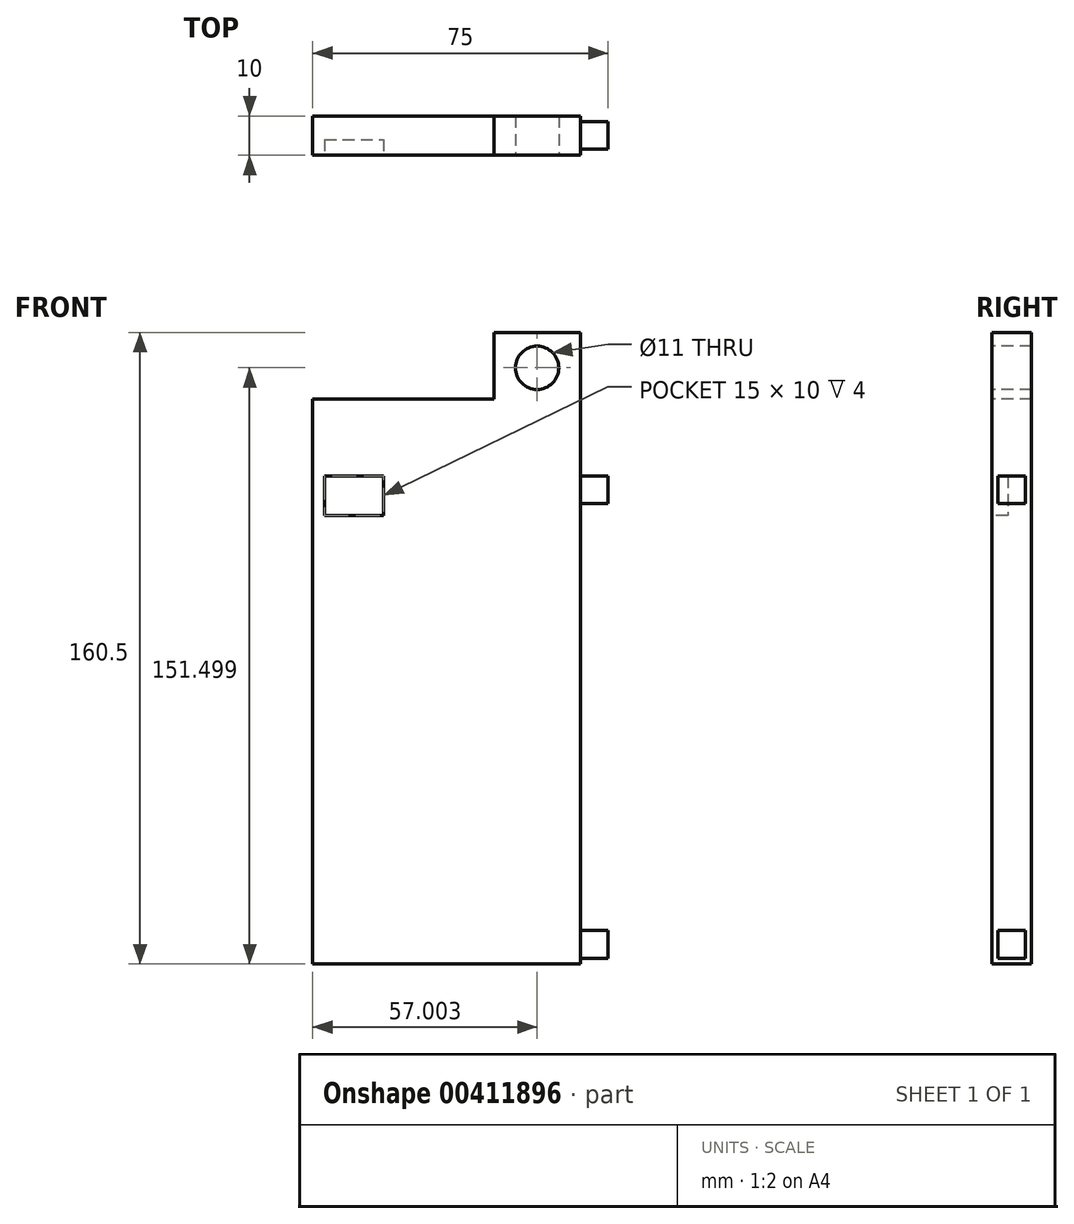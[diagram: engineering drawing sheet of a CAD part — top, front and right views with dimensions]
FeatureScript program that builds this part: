
annotation { "Feature Type Name" : "Feature", "Feature Type Description" : "" }
export const myFeature = defineFeature(function(context is Context, id is Id, definition is map)
    precondition{}
    {
        {
            var Q0;
            Q0=qCreatedBy(makeId("Front.planeOp"),FACE);
            var sketch = newSketch(context, id + "F0", { "sketchPlane" : qUnion([Q0])});
            skLineSegment(sketch, "E0.bottom", {"start": v(-29.83, 107.13) * mm, "end": v(38.17, 107.13) * mm});
            skLineSegment(sketch, "E0.top", {"start": v(-29.83, -53.37) * mm, "end": v(38.17, -53.37) * mm});
            skLineSegment(sketch, "E0.left", {"start": v(-29.83, 107.13) * mm, "end": v(-29.83, -53.37) * mm});
            skLineSegment(sketch, "E0.right", {"start": v(38.17, 107.13) * mm, "end": v(38.17, -53.37) * mm});
            skSolve(sketch);
        }
        {
            var Q0;
            Q0=makeQuery(id+"F0.imprint","IMPRINT",FACE,{"disambiguationData":[TD([[makeQuery(id+"F0.imprint","IMPRINT",EDGE,{"derivedFrom":sQuery(id+"F0.wireOp",EDGE,"E0.bottom")}),-1.0]])]});
            extrude(context, id + "F1", {"entities" : qUnion([Q0]), "depth" : 10 * mm});
        }
        {
            var Q0;
            Q0=makeQuery(id+"F1.opExtrude","CAP_FACE",FACE,{"disambiguationData":[OSD([sQuery(id+"F0.wireOp",EDGE,"E0.bottom"),sQuery(id+"F0.wireOp",EDGE,"E0.top"),sQuery(id+"F0.wireOp",EDGE,"E0.left"),sQuery(id+"F0.wireOp",EDGE,"E0.right")])],"isStart":false});
            var sketch = newSketch(context, id + "F2", { "sketchPlane" : qUnion([Q0])});
            skLineSegment(sketch, "E1.bottom", {"start": v(-29.83, 107.13) * mm, "end": v(16.17, 107.13) * mm});
            skLineSegment(sketch, "E1.top", {"start": v(-29.83, 90.13) * mm, "end": v(16.17, 90.13) * mm});
            skLineSegment(sketch, "E1.left", {"start": v(-29.83, 107.13) * mm, "end": v(-29.83, 90.13) * mm});
            skLineSegment(sketch, "E1.right", {"start": v(16.17, 107.13) * mm, "end": v(16.17, 90.13) * mm});
            skSolve(sketch);
        }
        {
            var Q0;
            Q0 = qSketchRegion(id + "F2", true);
            extrude(context, id + "F3", {"entities" : qUnion([Q0]), "operationType" : NewBodyOperationType.REMOVE, "oppositeDirection" : true, "depth" : 25 * mm});
        }
        {
            var Q0;
            Q0=makeQuery(id+"F1.opExtrude","CAP_FACE",FACE,{"disambiguationData":[OSD([sQuery(id+"F0.wireOp",EDGE,"E0.bottom"),sQuery(id+"F0.wireOp",EDGE,"E0.top"),sQuery(id+"F0.wireOp",EDGE,"E0.left"),sQuery(id+"F0.wireOp",EDGE,"E0.right")])],"isStart":false});
            var sketch = newSketch(context, id + "F4", { "sketchPlane" : qUnion([Q0])});
            skCircle(sketch, "E2", {"center": v(27.17, 98.13) * mm, "radius": 5.5 * mm});
            skSolve(sketch);
        }
        {
            var Q0;
            Q0=makeQuery(id+"F4.imprint","IMPRINT",FACE,{"disambiguationData":[TD([[makeQuery(id+"F4.imprint","IMPRINT",EDGE,{"derivedFrom":sQuery(id+"F4.wireOp",EDGE,"E2")}),1.0]])]});
            extrude(context, id + "F5", {"entities" : qUnion([Q0]), "operationType" : NewBodyOperationType.REMOVE, "oppositeDirection" : true, "depth" : 25 * mm});
        }
        {
            var Q0;
            Q0=makeQuery(id+"F1.opExtrude","CAP_FACE",FACE,{"disambiguationData":[OSD([sQuery(id+"F0.wireOp",EDGE,"E0.bottom"),sQuery(id+"F0.wireOp",EDGE,"E0.top"),sQuery(id+"F0.wireOp",EDGE,"E0.left"),sQuery(id+"F0.wireOp",EDGE,"E0.right")])],"isStart":false});
            var sketch = newSketch(context, id + "F6", { "sketchPlane" : qUnion([Q0])});
            skLineSegment(sketch, "E3.0.0", {"start": v(38.17, 107.13) * mm, "end": v(16.17, 107.13) * mm});
            skLineSegment(sketch, "E3.0.1", {"start": v(16.17, 107.13) * mm, "end": v(16.17, 90.13) * mm});
            skLineSegment(sketch, "E3.0.2", {"start": v(16.17, 90.13) * mm, "end": v(-29.83, 90.13) * mm});
            skLineSegment(sketch, "E3.0.3", {"start": v(-29.83, 90.13) * mm, "end": v(-29.83, -53.37) * mm});
            skLineSegment(sketch, "E3.0.4", {"start": v(-29.83, -53.37) * mm, "end": v(38.17, -53.37) * mm});
            skLineSegment(sketch, "E3.0.5", {"start": v(38.17, -53.37) * mm, "end": v(38.17, 107.13) * mm});
            skLineSegment(sketch, "E4.bottom", {"start": v(-26.83, 70.63) * mm, "end": v(-11.83, 70.63) * mm});
            skLineSegment(sketch, "E4.top", {"start": v(-26.83, 60.63) * mm, "end": v(-11.83, 60.63) * mm});
            skLineSegment(sketch, "E4.left", {"start": v(-26.83, 70.63) * mm, "end": v(-26.83, 60.63) * mm});
            skLineSegment(sketch, "E4.right", {"start": v(-11.83, 70.63) * mm, "end": v(-11.83, 60.63) * mm});
            skSolve(sketch);
        }
        {
            var Q0;
            Q0=makeQuery(id+"F6.imprint","IMPRINT",FACE,{"disambiguationData":[TD([[makeQuery(id+"F6.imprint","IMPRINT",EDGE,{"derivedFrom":sQuery(id+"F6.wireOp",EDGE,"E4.bottom")}),-1.0]])]});
            extrude(context, id + "F7", {"entities" : qUnion([Q0]), "operationType" : NewBodyOperationType.REMOVE, "oppositeDirection" : true, "depth" : 4 * mm});
        }
        {
            var Q0;
            Q0=makeQuery(id+"F1.opExtrude","SWEPT_FACE",FACE,{"disambiguationData":[OSD([sQuery(id+"F0.wireOp",EDGE,"E0.right")])]});
            var sketch = newSketch(context, id + "F8", { "sketchPlane" : qUnion([Q0])});
            skLineSegment(sketch, "E5.bottom", {"start": v(-8.5, -44.87) * mm, "end": v(-1.5, -44.87) * mm});
            skLineSegment(sketch, "E5.top", {"start": v(-8.5, -51.87) * mm, "end": v(-1.5, -51.87) * mm});
            skLineSegment(sketch, "E5.left", {"start": v(-8.5, -44.87) * mm, "end": v(-8.5, -51.87) * mm});
            skLineSegment(sketch, "E5.right", {"start": v(-1.5, -44.87) * mm, "end": v(-1.5, -51.87) * mm});
            skLineSegment(sketch, "E6.bottom", {"start": v(-8.5, 70.63) * mm, "end": v(-1.5, 70.63) * mm});
            skLineSegment(sketch, "E6.top", {"start": v(-8.5, 63.63) * mm, "end": v(-1.5, 63.63) * mm});
            skLineSegment(sketch, "E6.left", {"start": v(-8.5, 70.63) * mm, "end": v(-8.5, 63.63) * mm});
            skLineSegment(sketch, "E6.right", {"start": v(-1.5, 70.63) * mm, "end": v(-1.5, 63.63) * mm});
            skSolve(sketch);
        }
        {
            var Q0;
            Q0 = qSketchRegion(id + "F8", true);
            extrude(context, id + "F9", {"entities" : qUnion([Q0]), "operationType" : NewBodyOperationType.ADD, "depth" : 7 * mm});
        }
    });
